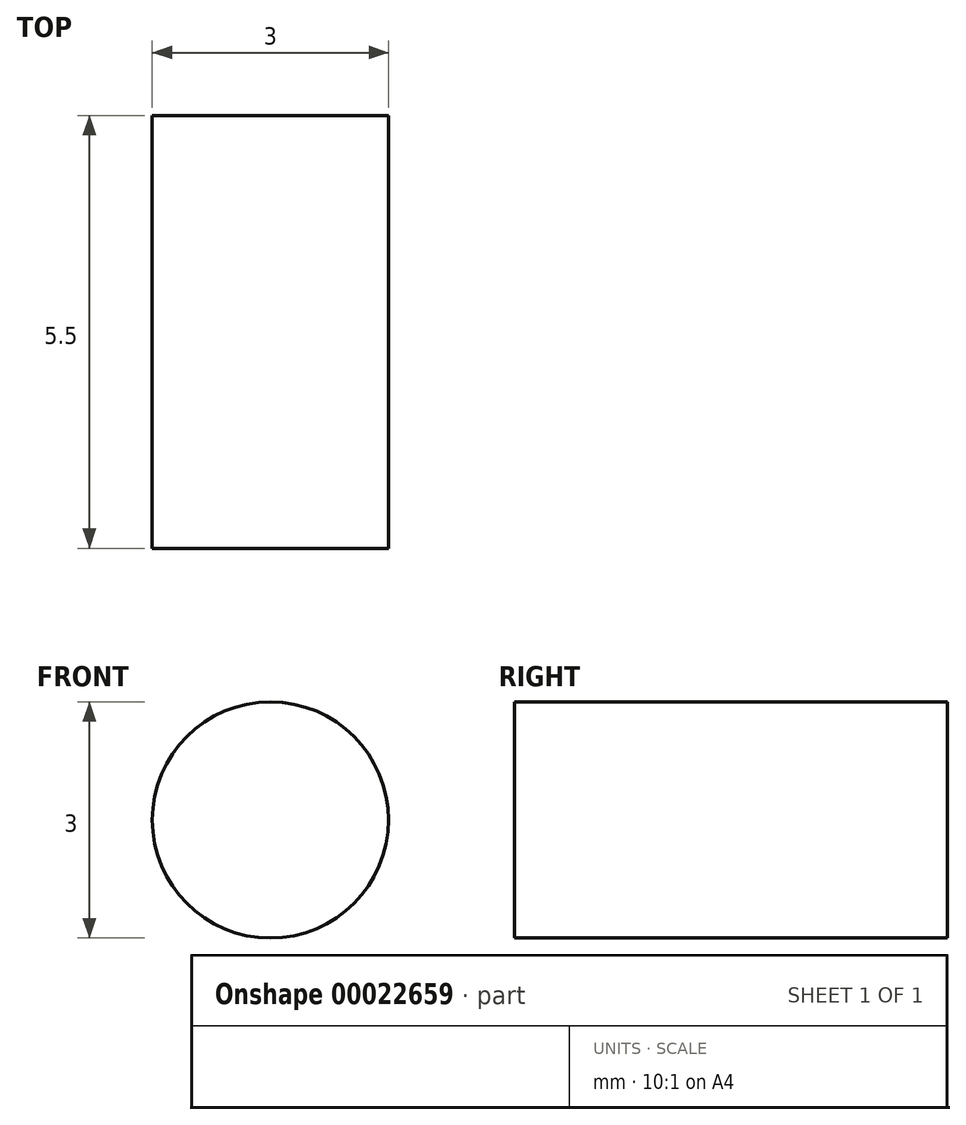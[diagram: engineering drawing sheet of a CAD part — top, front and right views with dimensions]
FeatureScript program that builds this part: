
annotation { "Feature Type Name" : "Feature", "Feature Type Description" : "" }
export const myFeature = defineFeature(function(context is Context, id is Id, definition is map)
    precondition{}
    {
        {
            var Q0;
            Q0=qCreatedBy(makeId("Front.planeOp"),FACE);
            var sketch = newSketch(context, id + "F0", { "sketchPlane" : qUnion([Q0])});
            skCircle(sketch, "E0", {"center": v(0, 0) * mm, "radius": 1.5 * mm});
            skSolve(sketch);
        }
        {
            var Q0;
            Q0=makeQuery(id+"F0.imprint","IMPRINT",FACE,{"disambiguationData":[TD([[makeQuery(id+"F0.imprint","IMPRINT",EDGE,{"derivedFrom":sQuery(id+"F0.wireOp",EDGE,"E0")}),1.0]])]});
            extrude(context, id + "F1", {"entities" : qUnion([Q0]), "depth" : 5.5 * mm});
        }
    });
